annotation { "Feature Type Name" : "Feature", "Feature Type Description" : "" }
export const myFeature = defineFeature(function(context is Context, id is Id, definition is map)
    precondition{}
    {
        {
            var Q0;
            Q0=qCreatedBy(makeId("Front.planeOp"),FACE);
            var sketch = newSketch(context, id + "F0", { "sketchPlane" : qUnion([Q0])});
            skLineSegment(sketch, "E0.bottom", {"start": v(14.6, 96.37) * mm, "end": v(-14.6, 96.37) * mm});
            skLineSegment(sketch, "E0.top", {"start": v(14.6, -96.37) * mm, "end": v(-14.6, -96.37) * mm});
            skLineSegment(sketch, "E0.left", {"start": v(20.96, 90.02) * mm, "end": v(20.96, 4.45) * mm});
            skLineSegment(sketch, "E0.right", {"start": v(-20.95, 90.02) * mm, "end": v(-20.95, 4.45) * mm});
            skPoint(sketch, "E0.middle", {"position": v(0, 0) * mm});
            skArc(sketch, "E1", {"start": v(-20.95, 90.02) * mm, "mid": v(-16.46, 91.88) * mm, "end": v(-14.6, 96.37) * mm});
            skArc(sketch, "E2", {"start": v(14.6, 96.37) * mm, "mid": v(16.46, 91.88) * mm, "end": v(20.96, 90.02) * mm});
            skArc(sketch, "E3", {"start": v(-14.6, -96.37) * mm, "mid": v(-16.46, -91.88) * mm, "end": v(-20.95, -90.02) * mm});
            skArc(sketch, "E4", {"start": v(20.96, -90.02) * mm, "mid": v(16.46, -91.88) * mm, "end": v(14.6, -96.37) * mm});
            skArc(sketch, "E5", {"start": v(-20.95, -4.44) * mm, "mid": v(-16.5, 0) * mm, "end": v(-20.95, 4.45) * mm});
            skArc(sketch, "E6", {"start": v(20.96, 4.45) * mm, "mid": v(16.51, 0) * mm, "end": v(20.96, -4.44) * mm});
            skLineSegment(sketch, "E7.trimOffspring", {"start": v(-20.95, -4.44) * mm, "end": v(-20.95, -90.02) * mm});
            skLineSegment(sketch, "E8.trimOffspring", {"start": v(20.96, -4.44) * mm, "end": v(20.96, -90.02) * mm});
            skSolve(sketch);
        }
        {
            var Q0;
            Q0=makeQuery(id+"F0.imprint","IMPRINT",FACE,{"disambiguationData":[TD([[makeQuery(id+"F0.imprint","IMPRINT",EDGE,{"derivedFrom":sQuery(id+"F0.wireOp",EDGE,"E0.bottom")}),1.0]])]});
            extrude(context, id + "F1", {"entities" : qUnion([Q0]), "depth" : 1.59 * mm, "offsetDistance" : 25.4 * mm});
        }
        {
            var Q0;
            Q0=makeQuery(id+"F1.opExtrude","CAP_FACE",FACE,{"disambiguationData":[OSD([sQuery(id+"F0.wireOp",EDGE,"E0.bottom"),sQuery(id+"F0.wireOp",EDGE,"E0.top"),sQuery(id+"F0.wireOp",EDGE,"E0.left"),sQuery(id+"F0.wireOp",EDGE,"E0.right"),sQuery(id+"F0.wireOp",EDGE,"E1"),sQuery(id+"F0.wireOp",EDGE,"E2"),sQuery(id+"F0.wireOp",EDGE,"E3"),sQuery(id+"F0.wireOp",EDGE,"E4"),sQuery(id+"F0.wireOp",EDGE,"E5"),sQuery(id+"F0.wireOp",EDGE,"E6"),sQuery(id+"F0.wireOp",EDGE,"E7.trimOffspring"),sQuery(id+"F0.wireOp",EDGE,"E8.trimOffspring")])],"isStart":false});
            var sketch = newSketch(context, id + "F2", { "sketchPlane" : qUnion([Q0])});
            skLineSegment(sketch, "E9", {"start": v(-46.49, 0) * mm, "end": v(75.13, 0) * mm});
            skLineSegment(sketch, "E10.0.1.0", {"start": v(-46.49, 13.74) * mm, "end": v(75.13, 13.74) * mm});
            skLineSegment(sketch, "E10.0.2.0", {"start": v(-46.49, 27.48) * mm, "end": v(75.13, 27.48) * mm});
            skLineSegment(sketch, "E10.0.3.0", {"start": v(-46.49, 41.22) * mm, "end": v(75.13, 41.22) * mm});
            skLineSegment(sketch, "E10.0.4.0", {"start": v(-46.49, 54.97) * mm, "end": v(75.13, 54.97) * mm});
            skLineSegment(sketch, "E10.0.5.0", {"start": v(-46.49, 68.7) * mm, "end": v(75.13, 68.7) * mm});
            skLineSegment(sketch, "E10.0.6.0", {"start": v(-46.49, 82.45) * mm, "end": v(75.13, 82.45) * mm});
            skLineSegment(sketch, "E10.direction1", {"start": v(-46.49, 0) * mm, "end": v(-21.09, 0) * mm, "construction": true});
            skLineSegment(sketch, "E10.direction2", {"start": v(-46.49, 0) * mm, "end": v(-46.49, 13.74) * mm, "construction": true});
            skLineSegment(sketch, "E11", {"start": v(0, 96.37) * mm, "end": v(0, 82.45) * mm});
            skCircle(sketch, "E12.cCircle", {"center": v(7.39, 87.72) * mm, "radius": 2.3 * mm, "construction": true});
            skLineSegment(sketch, "E12.0", {"start": v(5.08, 83.72) * mm, "end": v(5.08, 91.72) * mm});
            skLineSegment(sketch, "E12.1", {"start": v(5.08, 91.72) * mm, "end": v(12, 87.72) * mm});
            skLineSegment(sketch, "E12.2", {"start": v(12, 87.72) * mm, "end": v(5.08, 83.72) * mm});
            skPoint(sketch, "E12.0.midPoint", {"position": v(5.08, 87.72) * mm});
            skLineSegment(sketch, "E13.MirrorCS", {"start": v(-5.08, 91.72) * mm, "end": v(-12, 87.72) * mm});
            skLineSegment(sketch, "E14.MirrorCS", {"start": v(-5.08, 83.72) * mm, "end": v(-5.08, 91.72) * mm});
            skLineSegment(sketch, "E15.MirrorCS", {"start": v(-12, 87.72) * mm, "end": v(-5.08, 83.72) * mm});
            skSolve(sketch);
        }
        {
            var Q0;
            Q0=makeQuery(id+"F2.imprint","IMPRINT",FACE,{"disambiguationData":[TD([[makeQuery(id+"F2.imprint","IMPRINT",EDGE,{"derivedFrom":sQuery(id+"F2.wireOp",EDGE,"E13.MirrorCS")}),1.0]])]});
            var Q1;
            Q1=makeQuery(id+"F2.imprint","IMPRINT",FACE,{"disambiguationData":[TD([[makeQuery(id+"F2.imprint","IMPRINT",EDGE,{"derivedFrom":sQuery(id+"F2.wireOp",EDGE,"E12.0")}),-1.0]])]});
            extrude(context, id + "F3", {"entities" : qUnion([Q0, Q1]), "operationType" : NewBodyOperationType.REMOVE, "oppositeDirection" : true, "depth" : 25.4 * mm, "offsetDistance" : 25.4 * mm});
        }
        {
            var Q0;
            {var subQ1=makeQuery(id+"F1.opExtrude","CAP_EDGE",EDGE,{"disambiguationData":[OSD([sQuery(id+"F0.wireOp",EDGE,"E0.left")])],"isStart":false});var subQ3=sQuery(id+"F2.wireOp",EDGE,"E10.0.5.0");var subQ4=makeQuery(id+"F2.imprint","INTERSECT",VERTEX,{"derivedFrom":[subQ1,subQ3]});Q0=makeQuery(id+"F2.imprint","IMPRINT",FACE,{"disambiguationData":[TD([[makeQuery(id+"F2.imprint","IMPRINT",EDGE,{"disambiguationData":[TD([[subQ4,1.0]])],"derivedFrom":subQ3}),1.0]])]});}
            var sketch = newSketch(context, id + "F4", { "sketchPlane" : qUnion([Q0])});
            skText(sketch, "E16", { "text": "PARKING", "fontName": "AllertaStencil-Regular.ttf"});
            const initialGuessF4  = {"E16": [-0.01584, 0.07283, 1, 0, 0.0053]};
            skSetInitialGuess(sketch, initialGuessF4);
            skSolve(sketch);
        }
        {
            var Q0;
            Q0 = qSketchRegion(id + "F4", true);
            extrude(context, id + "F5", {"entities" : qUnion([Q0]), "operationType" : NewBodyOperationType.REMOVE, "oppositeDirection" : true, "depth" : 25.4 * mm, "offsetDistance" : 25.4 * mm});
        }
        {
            var Q0;
            {var subQ0=sQuery(id+"F2.wireOp",EDGE,"E10.0.4.0");var subQ1=makeQuery(id+"F1.opExtrude","CAP_EDGE",EDGE,{"disambiguationData":[OSD([sQuery(id+"F0.wireOp",EDGE,"E0.left")])],"isStart":false});var subQ2=makeQuery(id+"F2.imprint","INTERSECT",VERTEX,{"derivedFrom":[subQ1,subQ0]});Q0=makeQuery(id+"F2.imprint","IMPRINT",FACE,{"disambiguationData":[TD([[makeQuery(id+"F2.imprint","IMPRINT",EDGE,{"disambiguationData":[TD([[subQ2,1.0]])],"derivedFrom":subQ0}),1.0]])]});}
            var sketch = newSketch(context, id + "F6", { "sketchPlane" : qUnion([Q0])});
            skText(sketch, "E17", { "text": "HEADLIGHTS", "fontName": "AllertaStencil-Regular.ttf"});
            const initialGuessF6  = {"E17": [-0.01604, 0.06031, 1, 0, 0.0036]};
            skSetInitialGuess(sketch, initialGuessF6);
            skSolve(sketch);
        }
        {
            var Q0;
            Q0 = qSketchRegion(id + "F6", true);
            extrude(context, id + "F7", {"entities" : qUnion([Q0]), "operationType" : NewBodyOperationType.REMOVE, "oppositeDirection" : true, "depth" : 25.4 * mm, "offsetDistance" : 25.4 * mm});
        }
        {
            var Q0;
            {var subQ0=sQuery(id+"F2.wireOp",EDGE,"E10.0.3.0");var subQ1=makeQuery(id+"F1.opExtrude","CAP_EDGE",EDGE,{"disambiguationData":[OSD([sQuery(id+"F0.wireOp",EDGE,"E0.left")])],"isStart":false});var subQ2=makeQuery(id+"F2.imprint","INTERSECT",VERTEX,{"derivedFrom":[subQ1,subQ0]});Q0=makeQuery(id+"F2.imprint","IMPRINT",FACE,{"disambiguationData":[TD([[makeQuery(id+"F2.imprint","IMPRINT",EDGE,{"disambiguationData":[TD([[subQ2,1.0]])],"derivedFrom":subQ0}),1.0]])]});}
            var sketch = newSketch(context, id + "F8", { "sketchPlane" : qUnion([Q0])});
            skText(sketch, "E18", { "text": "HIGH BEAMS", "fontName": "AllertaStencil-Regular.ttf"});
            const initialGuessF8  = {"E18": [-0.01631, 0.04619, 1, 0, 0.00372]};
            skSetInitialGuess(sketch, initialGuessF8);
            skSolve(sketch);
        }
        {
            var Q0;
            Q0 = qSketchRegion(id + "F8", true);
            extrude(context, id + "F9", {"entities" : qUnion([Q0]), "operationType" : NewBodyOperationType.REMOVE, "oppositeDirection" : true, "depth" : 25.4 * mm, "offsetDistance" : 25.4 * mm});
        }
        {
            var Q0;
            {var subQ0=sQuery(id+"F2.wireOp",EDGE,"E10.0.2.0");var subQ1=makeQuery(id+"F1.opExtrude","CAP_EDGE",EDGE,{"disambiguationData":[OSD([sQuery(id+"F0.wireOp",EDGE,"E0.left")])],"isStart":false});var subQ2=makeQuery(id+"F2.imprint","INTERSECT",VERTEX,{"derivedFrom":[subQ1,subQ0]});Q0=makeQuery(id+"F2.imprint","IMPRINT",FACE,{"disambiguationData":[TD([[makeQuery(id+"F2.imprint","IMPRINT",EDGE,{"disambiguationData":[TD([[subQ2,1.0]])],"derivedFrom":subQ0}),1.0]])]});}
            var sketch = newSketch(context, id + "F10", { "sketchPlane" : qUnion([Q0])});
            skText(sketch, "E19", { "text": "WINCH BAR", "fontName": "AllertaStencil-Regular.ttf"});
            skText(sketch, "E20", { "text": "FRONT BUMPER", "fontName": "AllertaStencil-Regular.ttf"});
            skText(sketch, "E21", { "text": "WINDSHIELD", "fontName": "AllertaStencil-Regular.ttf"});
            const initialGuessF10  = {"E19": [-0.01635, 0.03237, 1, 0, 0.00397], "E20": [-0.0162, 0.0187, 1, 0, 0.00299], "E21": [-0.01606, 0.00495, 1, 0, 0.00362]};
            skSetInitialGuess(sketch, initialGuessF10);
            skSolve(sketch);
        }
        {
            var Q0;
            Q0 = qSketchRegion(id + "F10", true);
            extrude(context, id + "F11", {"entities" : qUnion([Q0]), "operationType" : NewBodyOperationType.REMOVE, "oppositeDirection" : true, "depth" : 25.4 * mm, "offsetDistance" : 25.4 * mm});
        }
        {
            var Q0;
            Q0=makeQuery(id+"F2.imprint","IMPRINT",FACE,{"disambiguationData":[TD([[makeQuery(id+"F2.imprint","IMPRINT",EDGE,{"derivedFrom":makeQuery(id+"F1.opExtrude","CAP_EDGE",EDGE,{"disambiguationData":[OSD([sQuery(id+"F0.wireOp",EDGE,"E0.top")])],"isStart":false})}),-1.0]])]});
            var sketch = newSketch(context, id + "F12", { "sketchPlane" : qUnion([Q0])});
            skLineSegment(sketch, "E22", {"start": v(-31.64, -13.74) * mm, "end": v(41.88, -13.74) * mm});
            skLineSegment(sketch, "E23.0.1.0", {"start": v(-31.64, -27.48) * mm, "end": v(41.88, -27.48) * mm});
            skLineSegment(sketch, "E23.0.2.0", {"start": v(-31.64, -41.22) * mm, "end": v(41.88, -41.22) * mm});
            skLineSegment(sketch, "E23.0.3.0", {"start": v(-31.64, -54.97) * mm, "end": v(41.88, -54.97) * mm});
            skLineSegment(sketch, "E23.0.4.0", {"start": v(-31.64, -68.7) * mm, "end": v(41.88, -68.7) * mm});
            skLineSegment(sketch, "E23.0.5.0", {"start": v(-31.64, -82.45) * mm, "end": v(41.88, -82.45) * mm});
            skLineSegment(sketch, "E23.0.6.0", {"start": v(-31.64, -96.19) * mm, "end": v(41.88, -96.19) * mm});
            skLineSegment(sketch, "E23.0.7.0", {"start": v(-31.64, -109.93) * mm, "end": v(41.88, -109.93) * mm});
            skLineSegment(sketch, "E23.direction1", {"start": v(-31.64, -13.74) * mm, "end": v(-6.24, -13.74) * mm, "construction": true});
            skLineSegment(sketch, "E23.direction2", {"start": v(-31.64, -13.74) * mm, "end": v(-31.64, -27.48) * mm, "construction": true});
            skSolve(sketch);
        }
        {
            var Q0;
            {var subQ0=makeQuery(id+"F1.opExtrude","CAP_EDGE",EDGE,{"disambiguationData":[OSD([sQuery(id+"F0.wireOp",EDGE,"E7.trimOffspring")])],"isStart":false});var subQ10=sQuery(id+"F12.wireOp",EDGE,"E22");var subQ12=makeQuery(id+"F2.imprint","IMPRINT",EDGE,{"derivedFrom":subQ0});var subQ13=makeQuery(id+"F12.imprint","INTERSECT",VERTEX,{"derivedFrom":[subQ12,subQ10]});Q0=makeQuery(id+"F12.imprint","IMPRINT",FACE,{"disambiguationData":[TD([[makeQuery(id+"F12.imprint","IMPRINT",EDGE,{"disambiguationData":[TD([[subQ13,-1.0]])],"derivedFrom":subQ10}),1.0]])]});}
            var sketch = newSketch(context, id + "F13", { "sketchPlane" : qUnion([Q0])});
            skText(sketch, "E24", { "text": "MAIN BAR", "fontName": "AllertaStencil-Regular.ttf"});
            const initialGuessF13  = {"E24": [-0.01592, -0.0093, 1, 0, 0.00467]};
            skSetInitialGuess(sketch, initialGuessF13);
            skSolve(sketch);
        }
        {
            var Q0;
            Q0 = qSketchRegion(id + "F13", true);
            extrude(context, id + "F14", {"entities" : qUnion([Q0]), "operationType" : NewBodyOperationType.REMOVE, "oppositeDirection" : true, "depth" : 25.4 * mm, "offsetDistance" : 25.4 * mm});
        }
        {
            var Q0;
            {var subQ0=sQuery(id+"F12.wireOp",EDGE,"E22");var subQ1=makeQuery(id+"F2.imprint","IMPRINT",EDGE,{"derivedFrom":makeQuery(id+"F1.opExtrude","CAP_EDGE",EDGE,{"disambiguationData":[OSD([sQuery(id+"F0.wireOp",EDGE,"E7.trimOffspring")])],"isStart":false})});var subQ2=makeQuery(id+"F12.imprint","INTERSECT",VERTEX,{"derivedFrom":[subQ1,subQ0]});Q0=makeQuery(id+"F12.imprint","IMPRINT",FACE,{"disambiguationData":[TD([[makeQuery(id+"F12.imprint","IMPRINT",EDGE,{"disambiguationData":[TD([[subQ2,-1.0]])],"derivedFrom":subQ0}),-1.0]])]});}
            var sketch = newSketch(context, id + "F15", { "sketchPlane" : qUnion([Q0])});
            skText(sketch, "E25", { "text": "ROCK LIGHTS", "fontName": "AllertaStencil-Regular.ttf"});
            const initialGuessF15  = {"E25": [-0.01568, -0.02216, 1, 0, 0.00353]};
            skSetInitialGuess(sketch, initialGuessF15);
            skSolve(sketch);
        }
        {
            var Q0;
            Q0 = qSketchRegion(id + "F15", true);
            extrude(context, id + "F16", {"entities" : qUnion([Q0]), "operationType" : NewBodyOperationType.REMOVE, "oppositeDirection" : true, "depth" : 25.4 * mm, "offsetDistance" : 25.4 * mm});
        }
        {
            var Q0;
            {var subQ0=sQuery(id+"F12.wireOp",EDGE,"E23.0.1.0");var subQ1=makeQuery(id+"F2.imprint","IMPRINT",EDGE,{"derivedFrom":makeQuery(id+"F1.opExtrude","CAP_EDGE",EDGE,{"disambiguationData":[OSD([sQuery(id+"F0.wireOp",EDGE,"E7.trimOffspring")])],"isStart":false})});var subQ2=makeQuery(id+"F12.imprint","INTERSECT",VERTEX,{"derivedFrom":[subQ1,subQ0]});Q0=makeQuery(id+"F12.imprint","IMPRINT",FACE,{"disambiguationData":[TD([[makeQuery(id+"F12.imprint","IMPRINT",EDGE,{"disambiguationData":[TD([[subQ2,-1.0]])],"derivedFrom":subQ0}),-1.0]])]});}
            var sketch = newSketch(context, id + "F17", { "sketchPlane" : qUnion([Q0])});
            skText(sketch, "E26", { "text": "REVERSE", "fontName": "AllertaStencil-Regular.ttf"});
            const initialGuessF17  = {"E26": [-0.01573, -0.0369, 1, 0, 0.00522]};
            skSetInitialGuess(sketch, initialGuessF17);
            skSolve(sketch);
        }
        {
            var Q0;
            Q0 = qSketchRegion(id + "F17", true);
            extrude(context, id + "F18", {"entities" : qUnion([Q0]), "operationType" : NewBodyOperationType.REMOVE, "oppositeDirection" : true, "depth" : 25.4 * mm, "offsetDistance" : 25.4 * mm});
        }
        {
            var Q0;
            {var subQ0=sQuery(id+"F12.wireOp",EDGE,"E23.0.2.0");var subQ1=makeQuery(id+"F2.imprint","IMPRINT",EDGE,{"derivedFrom":makeQuery(id+"F1.opExtrude","CAP_EDGE",EDGE,{"disambiguationData":[OSD([sQuery(id+"F0.wireOp",EDGE,"E7.trimOffspring")])],"isStart":false})});var subQ2=makeQuery(id+"F12.imprint","INTERSECT",VERTEX,{"derivedFrom":[subQ1,subQ0]});Q0=makeQuery(id+"F12.imprint","IMPRINT",FACE,{"disambiguationData":[TD([[makeQuery(id+"F12.imprint","IMPRINT",EDGE,{"disambiguationData":[TD([[subQ2,-1.0]])],"derivedFrom":subQ0}),-1.0]])]});}
            var sketch = newSketch(context, id + "F19", { "sketchPlane" : qUnion([Q0])});
            skText(sketch, "E27", { "text": "FLOOR", "fontName": "AllertaStencil-Regular.ttf"});
            const initialGuessF19  = {"E27": [-0.0154, -0.05158, 1, 0, 0.00695]};
            skSetInitialGuess(sketch, initialGuessF19);
            skSolve(sketch);
        }
        {
            var Q0;
            Q0 = qSketchRegion(id + "F19", true);
            extrude(context, id + "F20", {"entities" : qUnion([Q0]), "operationType" : NewBodyOperationType.REMOVE, "oppositeDirection" : true, "depth" : 25.4 * mm, "offsetDistance" : 25.4 * mm});
        }
        {
            var Q0;
            {var subQ0=sQuery(id+"F12.wireOp",EDGE,"E23.0.3.0");var subQ1=makeQuery(id+"F2.imprint","IMPRINT",EDGE,{"derivedFrom":makeQuery(id+"F1.opExtrude","CAP_EDGE",EDGE,{"disambiguationData":[OSD([sQuery(id+"F0.wireOp",EDGE,"E7.trimOffspring")])],"isStart":false})});var subQ2=makeQuery(id+"F12.imprint","INTERSECT",VERTEX,{"derivedFrom":[subQ1,subQ0]});Q0=makeQuery(id+"F12.imprint","IMPRINT",FACE,{"disambiguationData":[TD([[makeQuery(id+"F12.imprint","IMPRINT",EDGE,{"disambiguationData":[TD([[subQ2,-1.0]])],"derivedFrom":subQ0}),-1.0]])]});}
            var sketch = newSketch(context, id + "F21", { "sketchPlane" : qUnion([Q0])});
            skText(sketch, "E28", { "text": "CO-PILOT", "fontName": "AllertaStencil-Regular.ttf"});
            const initialGuessF21  = {"E28": [-0.01584, -0.0645, 1, 0, 0.0048]};
            skSetInitialGuess(sketch, initialGuessF21);
            skSolve(sketch);
        }
        {
            var Q0;
            Q0 = qSketchRegion(id + "F21", true);
            extrude(context, id + "F22", {"entities" : qUnion([Q0]), "operationType" : NewBodyOperationType.REMOVE, "oppositeDirection" : true, "depth" : 25.4 * mm, "offsetDistance" : 25.4 * mm});
        }
        {
            var Q0;
            {var subQ0=sQuery(id+"F12.wireOp",EDGE,"E23.0.4.0");var subQ1=makeQuery(id+"F2.imprint","IMPRINT",EDGE,{"derivedFrom":makeQuery(id+"F1.opExtrude","CAP_EDGE",EDGE,{"disambiguationData":[OSD([sQuery(id+"F0.wireOp",EDGE,"E7.trimOffspring")])],"isStart":false})});var subQ2=makeQuery(id+"F12.imprint","INTERSECT",VERTEX,{"derivedFrom":[subQ1,subQ0]});Q0=makeQuery(id+"F12.imprint","IMPRINT",FACE,{"disambiguationData":[TD([[makeQuery(id+"F12.imprint","IMPRINT",EDGE,{"disambiguationData":[TD([[subQ2,-1.0]])],"derivedFrom":subQ0}),-1.0]])]});}
            var sketch = newSketch(context, id + "F23", { "sketchPlane" : qUnion([Q0])});
            skText(sketch, "E29", { "text": "L SIDE", "fontName": "AllertaStencil-Regular.ttf"});
            skText(sketch, "E30", { "text": "R SIDE", "fontName": "AllertaStencil-Regular.ttf"});
            const initialGuessF23  = {"E29": [-0.01589, -0.07988, 1, 0, 0.00754], "E30": [-0.0159, -0.09075, 1, 0, 0.00736]};
            skSetInitialGuess(sketch, initialGuessF23);
            skSolve(sketch);
        }
        {
            var Q0;
            Q0 = qSketchRegion(id + "F23", true);
            extrude(context, id + "F24", {"entities" : qUnion([Q0]), "operationType" : NewBodyOperationType.REMOVE, "oppositeDirection" : true, "depth" : 25.4 * mm, "offsetDistance" : 25.4 * mm});
        }
    });